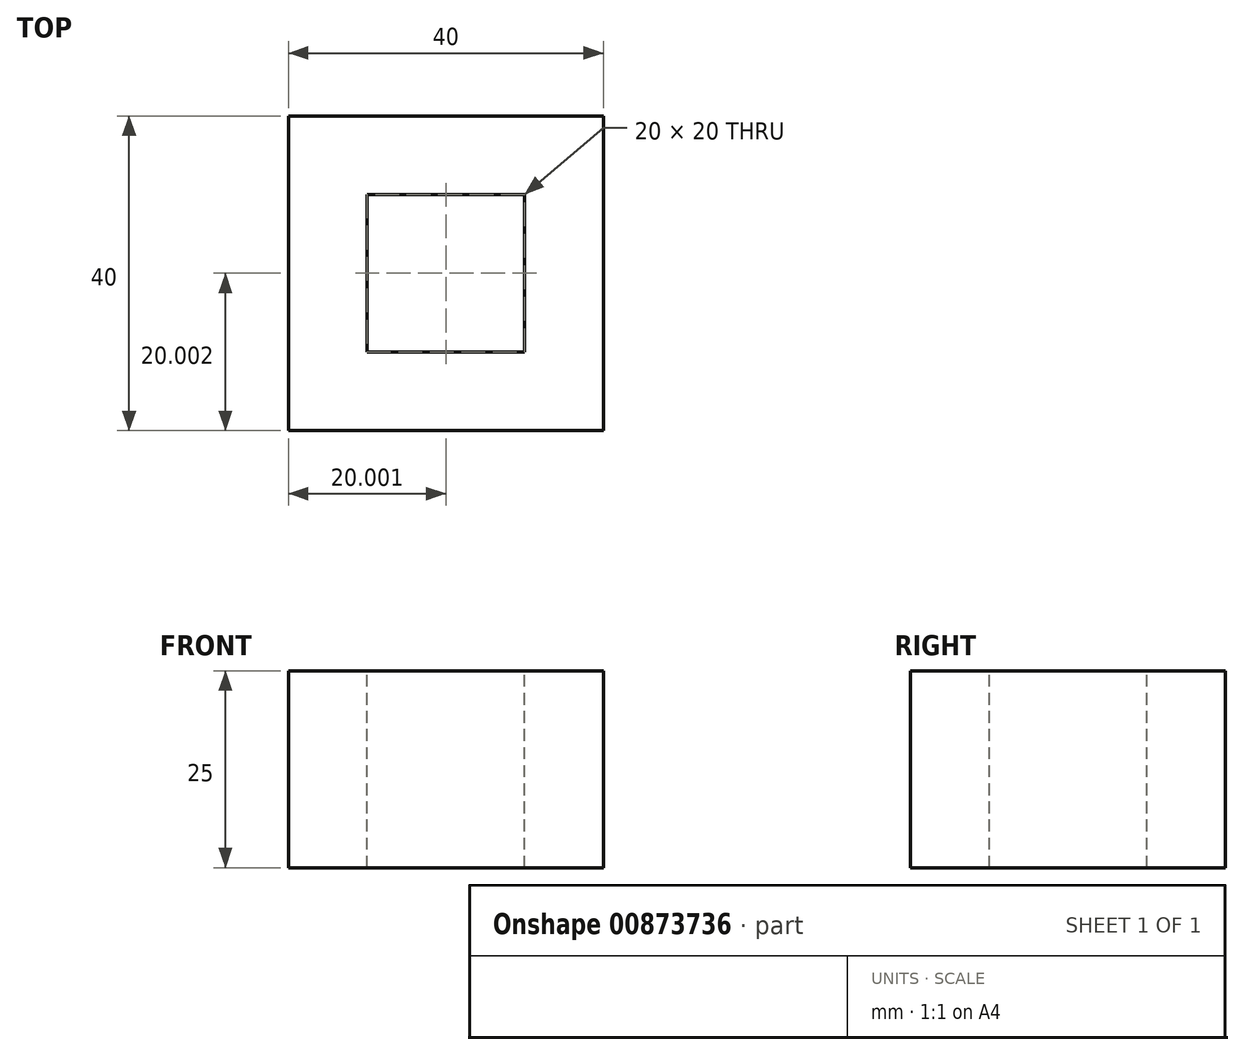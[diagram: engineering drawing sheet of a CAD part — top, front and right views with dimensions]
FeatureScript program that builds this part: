
annotation { "Feature Type Name" : "Feature", "Feature Type Description" : "" }
export const myFeature = defineFeature(function(context is Context, id is Id, definition is map)
    precondition{}
    {
        {
            var Q0;
            Q0=qCreatedBy(makeId("Top.planeOp"),FACE);
            var sketch = newSketch(context, id + "F0", { "sketchPlane" : qUnion([Q0])});
            skLineSegment(sketch, "E0.bottom", {"start": v(-21.1, 21.46) * mm, "end": v(18.9, 21.46) * mm});
            skLineSegment(sketch, "E0.top", {"start": v(-21.1, -18.54) * mm, "end": v(18.9, -18.54) * mm});
            skLineSegment(sketch, "E0.left", {"start": v(-21.1, 21.46) * mm, "end": v(-21.1, -18.54) * mm});
            skLineSegment(sketch, "E0.right", {"start": v(18.9, 21.46) * mm, "end": v(18.9, -18.54) * mm});
            skSolve(sketch);
        }
        {
            var Q0;
            Q0=makeQuery(id+"F0.imprint","IMPRINT",FACE,{"disambiguationData":[TD([[makeQuery(id+"F0.imprint","IMPRINT",EDGE,{"derivedFrom":sQuery(id+"F0.wireOp",EDGE,"E0.bottom")}),-1.0]])]});
            extrude(context, id + "F1", {"entities" : qUnion([Q0]), "depth" : 25 * mm, "offsetDistance" : 25 * mm});
        }
        {
            var Q0;
            Q0=makeQuery(id+"F1.opExtrude","CAP_FACE",FACE,{"disambiguationData":[OSD([sQuery(id+"F0.wireOp",EDGE,"E0.bottom"),sQuery(id+"F0.wireOp",EDGE,"E0.top"),sQuery(id+"F0.wireOp",EDGE,"E0.left"),sQuery(id+"F0.wireOp",EDGE,"E0.right")])],"isStart":false});
            var sketch = newSketch(context, id + "F2", { "sketchPlane" : qUnion([Q0])});
            skLineSegment(sketch, "E1.bottom", {"start": v(-11.1, 11.46) * mm, "end": v(8.9, 11.46) * mm});
            skLineSegment(sketch, "E1.top", {"start": v(-11.1, -8.54) * mm, "end": v(8.9, -8.54) * mm});
            skLineSegment(sketch, "E1.left", {"start": v(-11.1, 11.46) * mm, "end": v(-11.1, -8.54) * mm});
            skLineSegment(sketch, "E1.right", {"start": v(8.9, 11.46) * mm, "end": v(8.9, -8.54) * mm});
            skPoint(sketch, "E2", {"position": v(-1.1, 21.46) * mm});
            skPoint(sketch, "E3", {"position": v(-1.1, 11.46) * mm});
            skPoint(sketch, "E4", {"position": v(-21.1, 1.46) * mm});
            skPoint(sketch, "E5", {"position": v(-11.1, 1.46) * mm});
            skSolve(sketch);
        }
        {
            var Q0;
            Q0=makeQuery(id+"F2.imprint","IMPRINT",FACE,{"disambiguationData":[TD([[makeQuery(id+"F2.imprint","IMPRINT",EDGE,{"derivedFrom":sQuery(id+"F2.wireOp",EDGE,"E1.bottom")}),-1.0]])]});
            extrude(context, id + "F3", {"entities" : qUnion([Q0]), "operationType" : NewBodyOperationType.REMOVE, "oppositeDirection" : true, "depth" : 25 * mm, "offsetDistance" : 25 * mm});
        }
    });
